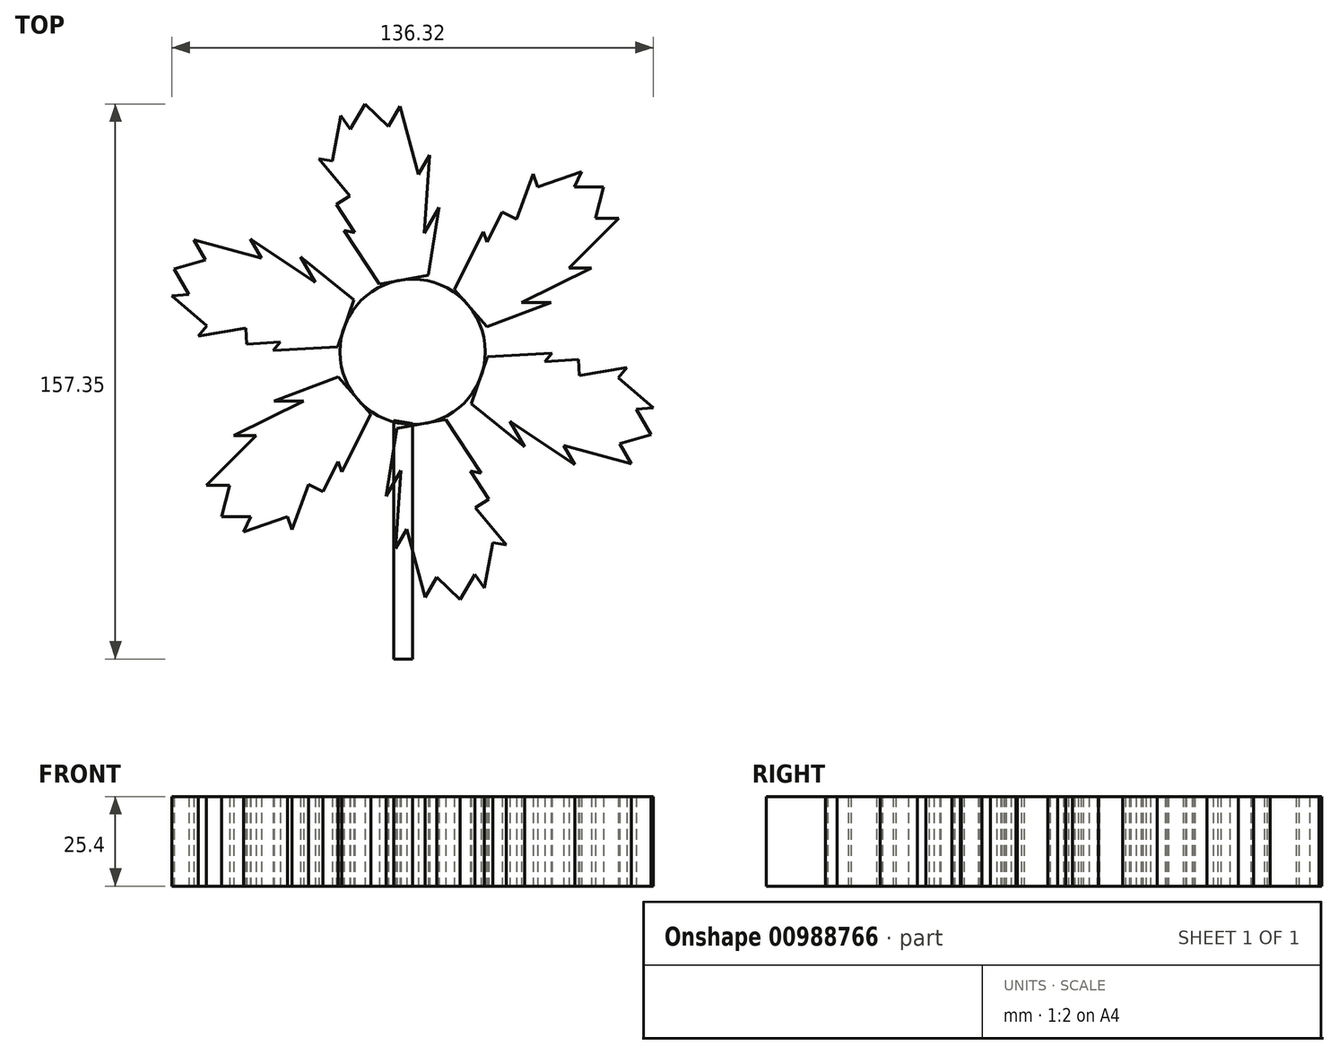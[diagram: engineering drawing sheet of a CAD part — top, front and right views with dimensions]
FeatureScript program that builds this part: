
annotation { "Feature Type Name" : "Feature", "Feature Type Description" : "" }
export const myFeature = defineFeature(function(context is Context, id is Id, definition is map)
    precondition{}
    {
        {
            var Q0;
            Q0=qCreatedBy(makeId("Top.planeOp"),FACE);
            var sketch = newSketch(context, id + "F0", { "sketchPlane" : qUnion([Q0])});
            skCircle(sketch, "E0", {"center": v(0, 0) * mm, "radius": 20.6 * mm});
            skSolve(sketch);
        }
        {
            var Q0;
            Q0=qCreatedBy(makeId("Top.planeOp"),FACE);
            var sketch = newSketch(context, id + "F1", { "sketchPlane" : qUnion([Q0])});
            skLineSegment(sketch, "E1", {"start": v(21.06, 7.06) * mm, "end": v(39.19, 13.97) * mm});
            skLineSegment(sketch, "E2", {"start": v(39.19, 13.97) * mm, "end": v(30.84, 13.97) * mm});
            skLineSegment(sketch, "E3", {"start": v(30.84, 13.97) * mm, "end": v(50.7, 23.75) * mm});
            skLineSegment(sketch, "E4", {"start": v(50.7, 23.75) * mm, "end": v(44.37, 23.75) * mm});
            skLineSegment(sketch, "E5", {"start": v(44.37, 23.75) * mm, "end": v(58.47, 37.86) * mm});
            skLineSegment(sketch, "E6", {"start": v(58.47, 37.86) * mm, "end": v(51.85, 37.86) * mm});
            skLineSegment(sketch, "E7", {"start": v(51.85, 37.86) * mm, "end": v(54.15, 46.78) * mm});
            skLineSegment(sketch, "E8", {"start": v(54.15, 46.78) * mm, "end": v(45.8, 46.78) * mm});
            skLineSegment(sketch, "E9", {"start": v(45.8, 46.78) * mm, "end": v(47.82, 51.1) * mm});
            skLineSegment(sketch, "E10", {"start": v(47.82, 51.1) * mm, "end": v(35.45, 46.78) * mm});
            skLineSegment(sketch, "E11", {"start": v(35.45, 46.78) * mm, "end": v(34.2, 50.37) * mm});
            skLineSegment(sketch, "E12", {"start": v(34.2, 50.37) * mm, "end": v(29.4, 37.57) * mm});
            skLineSegment(sketch, "E13", {"start": v(29.4, 37.57) * mm, "end": v(25.37, 39.58) * mm});
            skLineSegment(sketch, "E14", {"start": v(25.37, 39.58) * mm, "end": v(21.11, 31.06) * mm});
            skLineSegment(sketch, "E15", {"start": v(21.11, 31.06) * mm, "end": v(20.06, 34.08) * mm});
            skLineSegment(sketch, "E16", {"start": v(20.06, 34.08) * mm, "end": v(11.87, 17.7) * mm});
            skLineSegment(sketch, "E17", {"start": v(21.06, 7.06) * mm, "end": v(11.87, 17.7) * mm});
            skLineSegment(sketch, "E18.1.0", {"start": v(-21.6, 41.77) * mm, "end": v(-16.34, 33.82) * mm});
            skLineSegment(sketch, "E18.1.1", {"start": v(-20.34, 66.96) * mm, "end": v(-22.79, 54.09) * mm});
            skLineSegment(sketch, "E18.1.2", {"start": v(-19.48, 34.41) * mm, "end": v(-9.4, 19.13) * mm});
            skLineSegment(sketch, "E18.1.3", {"start": v(-13.43, 70.29) * mm, "end": v(-17.6, 63.06) * mm});
            skLineSegment(sketch, "E18.1.4", {"start": v(1.61, 50.3) * mm, "end": v(-3.55, 69.57) * mm});
            skLineSegment(sketch, "E18.1.5", {"start": v(-26.52, 54.8) * mm, "end": v(-17.83, 44.25) * mm});
            skLineSegment(sketch, "E18.1.6", {"start": v(-6.86, 63.83) * mm, "end": v(-13.43, 70.29) * mm});
            skLineSegment(sketch, "E18.1.7", {"start": v(-17.6, 63.06) * mm, "end": v(-20.34, 66.96) * mm});
            skLineSegment(sketch, "E18.1.8", {"start": v(3.32, 33.7) * mm, "end": v(4.78, 55.78) * mm});
            skLineSegment(sketch, "E18.1.9", {"start": v(4.78, 55.78) * mm, "end": v(1.61, 50.3) * mm});
            skLineSegment(sketch, "E18.1.10", {"start": v(-3.55, 69.57) * mm, "end": v(-6.86, 63.83) * mm});
            skLineSegment(sketch, "E18.1.11", {"start": v(-16.34, 33.82) * mm, "end": v(-19.48, 34.41) * mm});
            skLineSegment(sketch, "E18.1.12", {"start": v(-22.79, 54.09) * mm, "end": v(-26.52, 54.8) * mm});
            skLineSegment(sketch, "E18.1.13", {"start": v(-17.83, 44.25) * mm, "end": v(-21.6, 41.77) * mm});
            skLineSegment(sketch, "E18.1.14", {"start": v(7.5, 40.92) * mm, "end": v(3.32, 33.7) * mm});
            skLineSegment(sketch, "E18.1.15", {"start": v(4.41, 21.77) * mm, "end": v(7.5, 40.92) * mm});
            skLineSegment(sketch, "E18.1.16", {"start": v(4.41, 21.77) * mm, "end": v(-9.4, 19.13) * mm});
            skLineSegment(sketch, "E18.2.0", {"start": v(-46.97, 2.18) * mm, "end": v(-37.46, 2.75) * mm});
            skLineSegment(sketch, "E18.2.1", {"start": v(-68.16, 15.87) * mm, "end": v(-58.23, 7.3) * mm});
            skLineSegment(sketch, "E18.2.2", {"start": v(-39.55, 0.33) * mm, "end": v(-21.26, 1.43) * mm});
            skLineSegment(sketch, "E18.2.3", {"start": v(-67.59, 23.51) * mm, "end": v(-63.41, 16.28) * mm});
            skLineSegment(sketch, "E18.2.4", {"start": v(-42.75, 26.55) * mm, "end": v(-62.02, 31.7) * mm});
            skLineSegment(sketch, "E18.2.5", {"start": v(-60.72, 4.43) * mm, "end": v(-47.24, 6.68) * mm});
            skLineSegment(sketch, "E18.2.6", {"start": v(-58.7, 25.98) * mm, "end": v(-67.59, 23.51) * mm});
            skLineSegment(sketch, "E18.2.7", {"start": v(-63.41, 16.28) * mm, "end": v(-68.16, 15.87) * mm});
            skLineSegment(sketch, "E18.2.8", {"start": v(-27.52, 19.73) * mm, "end": v(-45.92, 32.03) * mm});
            skLineSegment(sketch, "E18.2.9", {"start": v(-45.92, 32.03) * mm, "end": v(-42.75, 26.55) * mm});
            skLineSegment(sketch, "E18.2.10", {"start": v(-62.02, 31.7) * mm, "end": v(-58.7, 25.98) * mm});
            skLineSegment(sketch, "E18.2.11", {"start": v(-37.46, 2.75) * mm, "end": v(-39.55, 0.33) * mm});
            skLineSegment(sketch, "E18.2.12", {"start": v(-58.23, 7.3) * mm, "end": v(-60.72, 4.43) * mm});
            skLineSegment(sketch, "E18.2.13", {"start": v(-47.24, 6.68) * mm, "end": v(-46.97, 2.18) * mm});
            skLineSegment(sketch, "E18.2.14", {"start": v(-31.7, 26.95) * mm, "end": v(-27.52, 19.73) * mm});
            skLineSegment(sketch, "E18.2.15", {"start": v(-16.64, 14.7) * mm, "end": v(-31.7, 26.95) * mm});
            skLineSegment(sketch, "E18.2.16", {"start": v(-16.64, 14.7) * mm, "end": v(-21.26, 1.43) * mm});
            skLineSegment(sketch, "E18.3.0", {"start": v(-25.37, -39.58) * mm, "end": v(-21.11, -31.06) * mm});
            skLineSegment(sketch, "E18.3.1", {"start": v(-47.82, -51.1) * mm, "end": v(-35.45, -46.78) * mm});
            skLineSegment(sketch, "E18.3.2", {"start": v(-20.06, -34.08) * mm, "end": v(-11.87, -17.7) * mm});
            skLineSegment(sketch, "E18.3.3", {"start": v(-54.15, -46.78) * mm, "end": v(-45.8, -46.78) * mm});
            skLineSegment(sketch, "E18.3.4", {"start": v(-44.37, -23.75) * mm, "end": v(-58.47, -37.86) * mm});
            skLineSegment(sketch, "E18.3.5", {"start": v(-34.2, -50.37) * mm, "end": v(-29.4, -37.57) * mm});
            skLineSegment(sketch, "E18.3.6", {"start": v(-51.85, -37.86) * mm, "end": v(-54.15, -46.78) * mm});
            skLineSegment(sketch, "E18.3.7", {"start": v(-45.8, -46.78) * mm, "end": v(-47.82, -51.1) * mm});
            skLineSegment(sketch, "E18.3.8", {"start": v(-30.84, -13.97) * mm, "end": v(-50.7, -23.75) * mm});
            skLineSegment(sketch, "E18.3.9", {"start": v(-50.7, -23.75) * mm, "end": v(-44.37, -23.75) * mm});
            skLineSegment(sketch, "E18.3.10", {"start": v(-58.47, -37.86) * mm, "end": v(-51.85, -37.86) * mm});
            skLineSegment(sketch, "E18.3.11", {"start": v(-21.11, -31.06) * mm, "end": v(-20.06, -34.08) * mm});
            skLineSegment(sketch, "E18.3.12", {"start": v(-35.45, -46.78) * mm, "end": v(-34.2, -50.37) * mm});
            skLineSegment(sketch, "E18.3.13", {"start": v(-29.4, -37.57) * mm, "end": v(-25.37, -39.58) * mm});
            skLineSegment(sketch, "E18.3.14", {"start": v(-39.19, -13.97) * mm, "end": v(-30.84, -13.97) * mm});
            skLineSegment(sketch, "E18.3.15", {"start": v(-21.06, -7.06) * mm, "end": v(-39.19, -13.97) * mm});
            skLineSegment(sketch, "E18.3.16", {"start": v(-21.06, -7.06) * mm, "end": v(-11.87, -17.7) * mm});
            skLineSegment(sketch, "E18.4.0", {"start": v(21.6, -41.77) * mm, "end": v(16.34, -33.82) * mm});
            skLineSegment(sketch, "E18.4.1", {"start": v(20.34, -66.96) * mm, "end": v(22.79, -54.09) * mm});
            skLineSegment(sketch, "E18.4.2", {"start": v(19.48, -34.41) * mm, "end": v(9.4, -19.13) * mm});
            skLineSegment(sketch, "E18.4.3", {"start": v(13.43, -70.29) * mm, "end": v(17.6, -63.06) * mm});
            skLineSegment(sketch, "E18.4.4", {"start": v(-1.61, -50.3) * mm, "end": v(3.55, -69.57) * mm});
            skLineSegment(sketch, "E18.4.5", {"start": v(26.52, -54.8) * mm, "end": v(17.83, -44.25) * mm});
            skLineSegment(sketch, "E18.4.6", {"start": v(6.86, -63.83) * mm, "end": v(13.43, -70.29) * mm});
            skLineSegment(sketch, "E18.4.7", {"start": v(17.6, -63.06) * mm, "end": v(20.34, -66.96) * mm});
            skLineSegment(sketch, "E18.4.8", {"start": v(-3.32, -33.7) * mm, "end": v(-4.78, -55.78) * mm});
            skLineSegment(sketch, "E18.4.9", {"start": v(-4.78, -55.78) * mm, "end": v(-1.61, -50.3) * mm});
            skLineSegment(sketch, "E18.4.10", {"start": v(3.55, -69.57) * mm, "end": v(6.86, -63.83) * mm});
            skLineSegment(sketch, "E18.4.11", {"start": v(16.34, -33.82) * mm, "end": v(19.48, -34.41) * mm});
            skLineSegment(sketch, "E18.4.12", {"start": v(22.79, -54.09) * mm, "end": v(26.52, -54.8) * mm});
            skLineSegment(sketch, "E18.4.13", {"start": v(17.83, -44.25) * mm, "end": v(21.6, -41.77) * mm});
            skLineSegment(sketch, "E18.4.14", {"start": v(-7.5, -40.92) * mm, "end": v(-3.32, -33.7) * mm});
            skLineSegment(sketch, "E18.4.15", {"start": v(-4.41, -21.77) * mm, "end": v(-7.5, -40.92) * mm});
            skLineSegment(sketch, "E18.4.16", {"start": v(-4.41, -21.77) * mm, "end": v(9.4, -19.13) * mm});
            skLineSegment(sketch, "E18.5.0", {"start": v(46.97, -2.18) * mm, "end": v(37.46, -2.75) * mm});
            skLineSegment(sketch, "E18.5.1", {"start": v(68.16, -15.87) * mm, "end": v(58.23, -7.3) * mm});
            skLineSegment(sketch, "E18.5.2", {"start": v(39.55, -0.33) * mm, "end": v(21.26, -1.43) * mm});
            skLineSegment(sketch, "E18.5.3", {"start": v(67.59, -23.51) * mm, "end": v(63.41, -16.28) * mm});
            skLineSegment(sketch, "E18.5.4", {"start": v(42.75, -26.55) * mm, "end": v(62.02, -31.7) * mm});
            skLineSegment(sketch, "E18.5.5", {"start": v(60.72, -4.43) * mm, "end": v(47.24, -6.68) * mm});
            skLineSegment(sketch, "E18.5.6", {"start": v(58.7, -25.98) * mm, "end": v(67.59, -23.51) * mm});
            skLineSegment(sketch, "E18.5.7", {"start": v(63.41, -16.28) * mm, "end": v(68.16, -15.87) * mm});
            skLineSegment(sketch, "E18.5.8", {"start": v(27.52, -19.73) * mm, "end": v(45.92, -32.03) * mm});
            skLineSegment(sketch, "E18.5.9", {"start": v(45.92, -32.03) * mm, "end": v(42.75, -26.55) * mm});
            skLineSegment(sketch, "E18.5.10", {"start": v(62.02, -31.7) * mm, "end": v(58.7, -25.98) * mm});
            skLineSegment(sketch, "E18.5.11", {"start": v(37.46, -2.75) * mm, "end": v(39.55, -0.33) * mm});
            skLineSegment(sketch, "E18.5.12", {"start": v(58.23, -7.3) * mm, "end": v(60.72, -4.43) * mm});
            skLineSegment(sketch, "E18.5.13", {"start": v(47.24, -6.68) * mm, "end": v(46.97, -2.18) * mm});
            skLineSegment(sketch, "E18.5.14", {"start": v(31.7, -26.95) * mm, "end": v(27.52, -19.73) * mm});
            skLineSegment(sketch, "E18.5.15", {"start": v(16.64, -14.7) * mm, "end": v(31.7, -26.95) * mm});
            skLineSegment(sketch, "E18.5.16", {"start": v(16.64, -14.7) * mm, "end": v(21.26, -1.43) * mm});
            skPoint(sketch, "E18.center", {"position": v(0, 0) * mm});
            skSolve(sketch);
        }
        {
            var Q0;
            Q0=makeQuery(id+"F1.imprint","IMPRINT",FACE,{"disambiguationData":[TD([[makeQuery(id+"F1.imprint","IMPRINT",EDGE,{"derivedFrom":sQuery(id+"F1.wireOp",EDGE,"E18.1.0")}),1.0]])]});
            var Q1;
            Q1=makeQuery(id+"F1.imprint","IMPRINT",FACE,{"disambiguationData":[TD([[makeQuery(id+"F1.imprint","IMPRINT",EDGE,{"derivedFrom":sQuery(id+"F1.wireOp",EDGE,"E18.2.0")}),1.0]])]});
            var Q2;
            Q2=makeQuery(id+"F0.imprint","IMPRINT",FACE,{"disambiguationData":[TD([[makeQuery(id+"F0.imprint","IMPRINT",EDGE,{"derivedFrom":sQuery(id+"F0.wireOp",EDGE,"E0")}),1.0]])]});
            var Q3;
            Q3=makeQuery(id+"F1.imprint","IMPRINT",FACE,{"disambiguationData":[TD([[makeQuery(id+"F1.imprint","IMPRINT",EDGE,{"derivedFrom":sQuery(id+"F1.wireOp",EDGE,"E1")}),1.0]])]});
            var Q4;
            Q4=makeQuery(id+"F1.imprint","IMPRINT",FACE,{"disambiguationData":[TD([[makeQuery(id+"F1.imprint","IMPRINT",EDGE,{"derivedFrom":sQuery(id+"F1.wireOp",EDGE,"E18.5.0")}),1.0]])]});
            var Q5;
            Q5=makeQuery(id+"F1.imprint","IMPRINT",FACE,{"disambiguationData":[TD([[makeQuery(id+"F1.imprint","IMPRINT",EDGE,{"derivedFrom":sQuery(id+"F1.wireOp",EDGE,"E18.4.0")}),1.0]])]});
            var Q6;
            Q6=makeQuery(id+"F1.imprint","IMPRINT",FACE,{"disambiguationData":[TD([[makeQuery(id+"F1.imprint","IMPRINT",EDGE,{"derivedFrom":sQuery(id+"F1.wireOp",EDGE,"E18.3.0")}),1.0]])]});
            extrude(context, id + "F2", {"entities" : qUnion([Q0, Q1, Q2, Q3, Q4, Q5, Q6]), "depth" : 25.4 * mm, "offsetDistance" : 25.4 * mm});
        }
        {
            var Q0;
            Q0=qCreatedBy(makeId("Top.planeOp"),FACE);
            var sketch = newSketch(context, id + "F3", { "sketchPlane" : qUnion([Q0])});
            skLineSegment(sketch, "E19", {"start": v(-5.32, -19.43) * mm, "end": v(-5.32, -87.06) * mm});
            skLineSegment(sketch, "E20", {"start": v(-5.32, -87.06) * mm, "end": v(0, -87.06) * mm});
            skLineSegment(sketch, "E21", {"start": v(0, -87.06) * mm, "end": v(0, -20.3) * mm});
            skLineSegment(sketch, "E22", {"start": v(-5.32, -19.43) * mm, "end": v(0, -20.3) * mm});
            skSolve(sketch);
        }
        {
            var Q0;
            Q0 = qSketchRegion(id + "F3", true);
            extrude(context, id + "F4", {"entities" : qUnion([Q0]), "depth" : 25.4 * mm, "offsetDistance" : 25.4 * mm});
        }
    });
